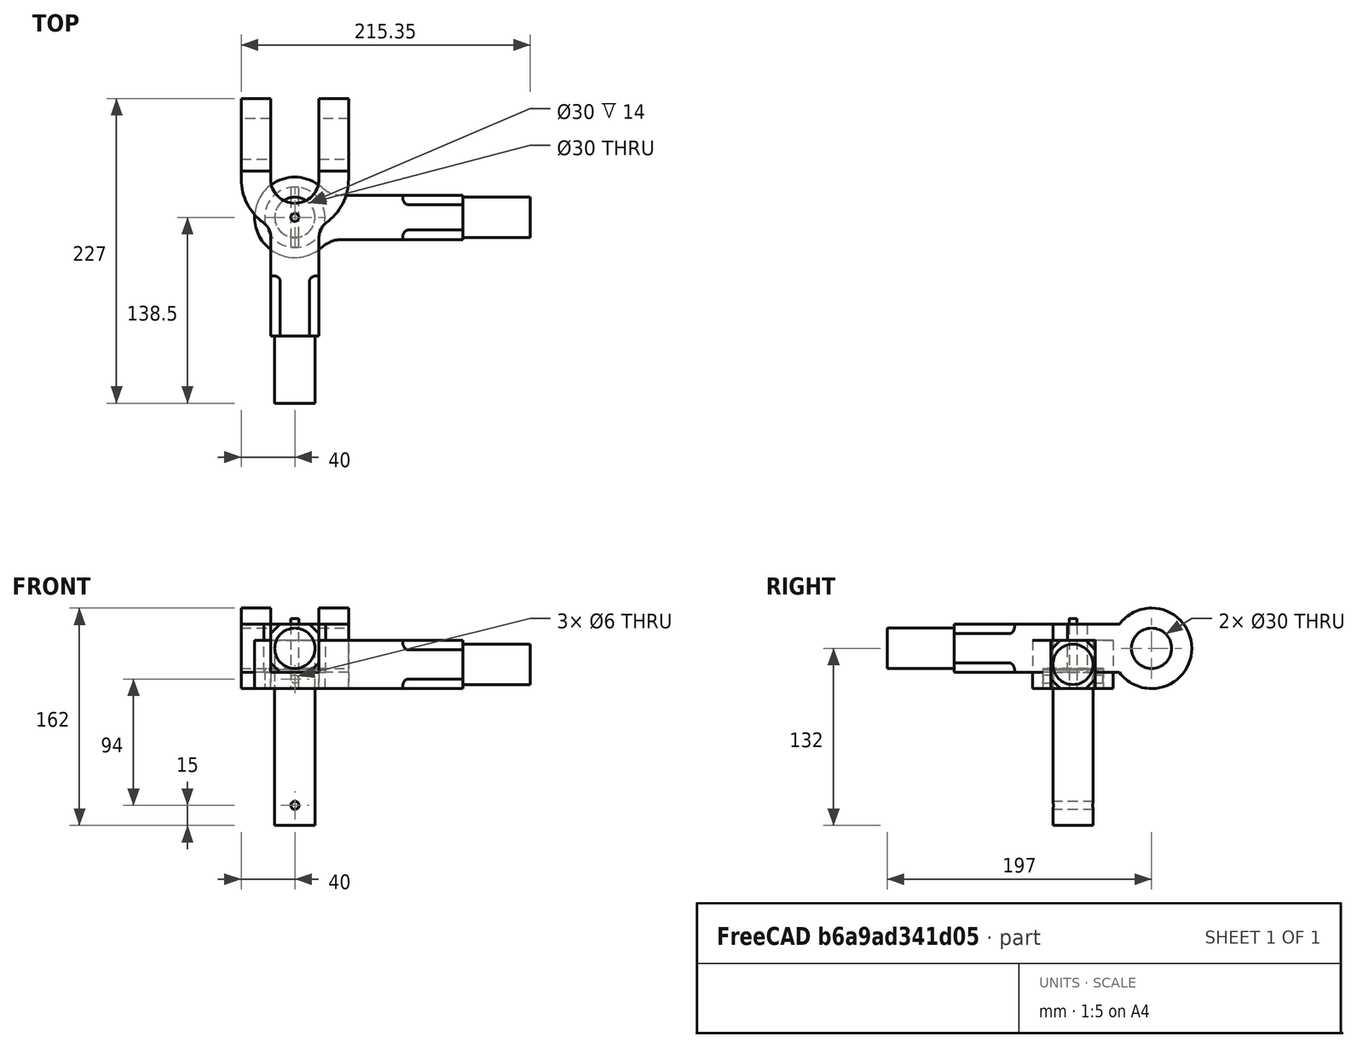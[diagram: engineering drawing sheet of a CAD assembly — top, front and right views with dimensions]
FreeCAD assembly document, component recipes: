
FREECAD ASSEMBLY — COMPONENT RECIPES ("kunckle joint assembly and parts")

This assembly document has 5 components, labeled P0..P4 below (a component is one placed body or linked part). 5 of them carry a construction recipe — the FreeCAD feature program that regenerates the part from scratch, quoted from this document or its linked companion documents; the rest are supplied as boundary geometry only. No exploded tour is included for this assembly.
COMPONENT P0 — recipe-attached ("Collar001", modeled in this document).
Construction recipe (the document's own serialized feature program — sketch geometry with constraints, then the solid features built on it; lengths are millimeters unless a unit is written):

FEATURE [Sketcher::SketchObject] Sketch002
  ArcFitTolerance = 1e-06
  AttachmentSupport = -> [XY_Plane001]
  FullyConstrained = true
  MakeInternals = false
  MapMode = 5
  sketch-geometry (2):
    g0: Circle CenterX=0 CenterY=0 CenterZ=0 NormalX=0 NormalY=0 NormalZ=1 AngleXU=0 Radius=22.5
    g1: Circle CenterX=0 CenterY=0 CenterZ=0 NormalX=0 NormalY=0 NormalZ=1 AngleXU=0 Radius=15
  constraints (4):
    c: Coincident(g0,g-1)
    c: Coincident(g1,g0)
    c: Diameter(g0) = 45
    c: Diameter(g1) = 30
FEATURE [PartDesign::Pad] Pad002
  Direction = (0,0,1)
  Length = 14
  Length2 = 10
  Profile = -> Sketch002
  ReferenceAxis = -> Sketch002 [N_Axis]
  Refine = true
  Suppressed = false
  Type = 0
FEATURE [Sketcher::SketchObject] Sketch003
  ArcFitTolerance = 1e-06
  AttachmentSupport = -> [XZ_Plane001]
  FullyConstrained = true
  MakeInternals = false
  MapMode = 5
  Placement = pos=(0,0,0) rot=(1,0,0;1.5708rad)
  sketch-geometry (1):
    g0: Circle CenterX=0 CenterY=7 CenterZ=0 NormalX=0 NormalY=0 NormalZ=1 AngleXU=0 Radius=3
  constraints (3):
    c: PointOnObject(g0,g-2)
    c: Diameter(g0) = 6
    c: DistanceY(g-1,g0) = 7
FEATURE [PartDesign::Pocket] Pocket
  BaseFeature = -> Pad002
  Direction = (0,1,-2e-16)
  Length = 5
  Length2 = 5
  Midplane = true
  Profile = -> Sketch003
  ReferenceAxis = -> Sketch003 [N_Axis]
  Refine = true
  Suppressed = false
  Type = 1
FEATURE [PartDesign::Body] Body001  label="Collar"
  AllowCompound = false
  Group = -> [Sketch002,Pad002,Sketch003,Pocket]
  Origin = -> Origin001
  Tip = -> Pocket
COMPONENT P1 — recipe-attached ("Single_eye001", modeled in this document).
Construction recipe (the document's own serialized feature program — sketch geometry with constraints, then the solid features built on it; lengths are millimeters unless a unit is written):

FEATURE [Sketcher::SketchObject] Sketch
  ArcFitTolerance = 1e-06
  AttachmentSupport = -> [XY_Plane]
  FullyConstrained = true
  MakeInternals = false
  MapMode = 5
  sketch-geometry (7):
    g0: ArcOfCircle CenterX=0 CenterY=0 CenterZ=0 NormalX=0 NormalY=0 NormalZ=1 AngleXU=0 Radius=30 StartAngle=0.840092 EndAngle=5.44179
    g1: Circle CenterX=0 CenterY=0 CenterZ=0 NormalX=0 NormalY=0 NormalZ=1 AngleXU=0 Radius=15
    g2: LineSegment StartX=35.3005 StartY=-16.5231 StartZ=0 EndX=125.352 EndY=-16.5231 EndZ=0
    g3: LineSegment StartX=125.352 StartY=-16.5231 StartZ=0 EndX=125.352 EndY=16.4769 EndZ=0
    g4: LineSegment StartX=125.352 StartY=16.4769 StartZ=0 EndX=35.3521 EndY=16.4769 EndZ=0
    g5: ArcOfCircle CenterX=35.3521 CenterY=39.4473 CenterZ=0 NormalX=0 NormalY=0 NormalZ=1 AngleXU=0 Radius=22.9703 StartAngle=3.98168 EndAngle=4.71239
    g6: ArcOfCircle CenterX=35.3005 CenterY=-39.4934 CenterZ=0 NormalX=0 NormalY=0 NormalZ=1 AngleXU=0 Radius=22.9703 StartAngle=1.5708 EndAngle=2.30019
  constraints (18):
    c: Coincident(g0,g-1)
    c: Coincident(g1,g0)
    c: Diameter(g1) = 30
    c: Diameter(g0) = 60
    c: Coincident(g2,g3)
    c: Coincident(g3,g4)
    c: Vertical(g3)
    c: Horizontal(g2)
    c: Horizontal(g4)
    c: DistanceY(g3,g3) = 33
    c: Tangent(g0,g5) = 1.5708
    c: Tangent(g4,g5) = 1.5708
    c: Tangent(g0,g6) = 1.5708
    c: Tangent(g2,g6) = 1.5708
    c: Equal(g5,g6)
    c: Block(g5)
    c: Block(g6)
    c: DistanceX(g4,g4) = 90
FEATURE [PartDesign::Pad] Pad
  Direction = (0,0,1)
  Length = 36
  Length2 = 10
  Profile = -> Sketch
  ReferenceAxis = -> Sketch [N_Axis]
  Refine = true
  Suppressed = false
  Type = 0
FEATURE [Sketcher::SketchObject] Sketch001
  ArcFitTolerance = 1e-06
  AttachmentSupport = -> [Pad]
  ExternalGeometry = -> [Pad]
  FullyConstrained = true
  MakeInternals = false
  MapMode = 5
  Placement = pos=(125.352,0,0) rot=(0.57735,0.57735,0.57735;2.0944rad)
  sketch-geometry (1):
    g0: Circle CenterX=-0.0230899 CenterY=18 CenterZ=0 NormalX=0 NormalY=0 NormalZ=1 AngleXU=0 Radius=15
  constraints (2):
    c: Diameter(g0) = 30
    c: Symmetric(g-4,g-3,g0)
FEATURE [PartDesign::Pad] Pad001
  BaseFeature = -> Pad
  Direction = (1,0,0)
  Length = 50
  Length2 = 10
  Profile = -> Sketch001
  ReferenceAxis = -> Sketch001 [N_Axis]
  Refine = true
  Suppressed = false
  Type = 0
FEATURE [Sketcher::SketchObject] Sketch008
  ArcFitTolerance = 1e-06
  AttachmentSupport = -> [Pad001]
  ExternalGeometry = -> [Pad001]
  FullyConstrained = true
  MakeInternals = false
  MapMode = 5
  Placement = pos=(125.352,0,0) rot=(0.57735,0.57735,0.57735;2.0944rad)
  sketch-geometry (12):
    g0: LineSegment StartX=-16.5231 StartY=36 StartZ=0 EndX=-16.5231 EndY=28.9289 EndZ=0
    g1: LineSegment StartX=-16.5231 StartY=28.9289 StartZ=0 EndX=-9.45202 EndY=36 EndZ=0
    g2: LineSegment StartX=-16.5231 StartY=36 StartZ=0 EndX=-9.45202 EndY=36 EndZ=0
    g3: LineSegment StartX=-16.5231 StartY=7.07107 StartZ=0 EndX=-16.5231 EndY=0 EndZ=0
    g4: LineSegment StartX=-16.5231 StartY=0 StartZ=0 EndX=-9.45202 EndY=0 EndZ=0
    g5: LineSegment StartX=-9.45202 StartY=0 StartZ=0 EndX=-16.5231 EndY=7.07107 EndZ=0
    g6: LineSegment StartX=16.5231 StartY=28.9753 StartZ=0 EndX=9.45202 EndY=36 EndZ=0
    g7: LineSegment StartX=16.4769 StartY=36 StartZ=0 EndX=9.45202 EndY=36 EndZ=0
    g8: LineSegment StartX=16.4769 StartY=36 StartZ=0 EndX=16.5231 EndY=28.9753 EndZ=0
    g9: LineSegment StartX=9.40584 StartY=0 StartZ=0 EndX=16.4769 EndY=7.07107 EndZ=0
    g10: LineSegment StartX=16.4769 StartY=7.07107 StartZ=0 EndX=16.4769 EndY=0 EndZ=0
    g11: LineSegment StartX=16.4769 StartY=0 StartZ=0 EndX=9.40584 EndY=0 EndZ=0
  constraints (30):
    c: Coincident(g0,g-5)
    c: PointOnObject(g0,g-5)
    c: Coincident(g1,g0)
    c: Coincident(g2,g0)
    c: Coincident(g2,g1)
    c: PointOnObject(g1,g-3)
    c: PointOnObject(g3,g-5)
    c: Coincident(g3,g-5)
    c: Coincident(g3,g4)
    c: PointOnObject(g4,g-1)
    c: Coincident(g4,g5)
    c: Coincident(g5,g3)
    c: Equal(g2,g0)
    c: Distance(g1,g1) = 10
    c: Distance(g5,g5) = 10
    c: Equal(g3,g4)
    c: Coincident(g6,g8)
    c: Coincident(g7,g8)
    c: Coincident(g7,g6)
    c: Equal(g7,g8)
    c: Coincident(g10,g11)
    c: Coincident(g11,g9)
    c: Coincident(g9,g10)
    c: Equal(g10,g11)
    c: Block(g6)
    c: Coincident(g10,g-4)
    c: PointOnObject(g9,g-1)
    c: Coincident(g7,g-4)
    c: PointOnObject(g9,g-4)
    c: Distance(g9,g9) = 10
FEATURE [PartDesign::Pocket] Pocket002
  BaseFeature = -> Pad001
  Direction = (-1,0,0)
  Length = 45
  Length2 = 5
  Profile = -> Sketch008
  ReferenceAxis = -> Sketch008 [N_Axis]
  Refine = true
  Suppressed = false
  Type = 0
FEATURE [PartDesign::Fillet] Fillet
  Base = -> Pocket002 [Edge46,Edge44]
  BaseFeature = -> Pocket002
  Radius = 4
  Refine = true
  SupportTransform = false
  Suppressed = false
  UseAllEdges = false
FEATURE [PartDesign::Fillet] Fillet001
  Base = -> Fillet [Edge36,Edge52]
  BaseFeature = -> Fillet
  Radius = 4
  Refine = true
  SupportTransform = false
  Suppressed = false
  UseAllEdges = false
FEATURE [PartDesign::Body] Body  label="Single_eye"
  AllowCompound = false
  Group = -> [Sketch,Pad,Sketch001,Pad001,Sketch008,Pocket002,Fillet,Fillet001]
  Origin = -> Origin
  Tip = -> Fillet001
COMPONENT P2 — recipe-attached ("double eye001", modeled in this document).
Construction recipe (the document's own serialized feature program — sketch geometry with constraints, then the solid features built on it; lengths are millimeters unless a unit is written):

FEATURE [Sketcher::SketchObject] Sketch009
  ArcFitTolerance = 1e-06
  AttachmentSupport = -> [XY_Plane004]
  FullyConstrained = true
  MakeInternals = false
  MapMode = 5
  sketch-geometry (5):
    g0: LineSegment StartX=-40 StartY=88.5 StartZ=0 EndX=-40 EndY=-88.5 EndZ=0
    g1: LineSegment StartX=-40 StartY=-88.5 StartZ=0 EndX=40 EndY=-88.5 EndZ=0
    g2: LineSegment StartX=40 StartY=-88.5 StartZ=0 EndX=40 EndY=88.5 EndZ=0
    g3: LineSegment StartX=40 StartY=88.5 StartZ=0 EndX=-40 EndY=88.5 EndZ=0
    g4: GeomPoint [constr] X=0 Y=0 Z=0
  constraints (12):
    c: Coincident(g0,g1)
    c: Coincident(g1,g2)
    c: Coincident(g2,g3)
    c: Coincident(g3,g0)
    c: Vertical(g0)
    c: Vertical(g2)
    c: Horizontal(g1)
    c: Horizontal(g3)
    c: Symmetric(g2,g0,g4)
    c: Coincident(g4,g-1)
    c: DistanceY(g2,g2) = 177
    c: DistanceX(g3,g3) = 80
FEATURE [PartDesign::Pad] Pad006
  Direction = (0,0,1)
  Length = 60
  Length2 = 10
  Profile = -> Sketch009
  ReferenceAxis = -> Sketch009 [N_Axis]
  Refine = true
  Suppressed = false
  Type = 0
FEATURE [PartDesign::Pad] Pad007
  BaseFeature = -> Pad006
  Direction = (0,0,1)
  Length = 5
  Length2 = 10
  Profile = -> Sketch009
  ReferenceAxis = -> Sketch009 [N_Axis]
  Refine = true
  Suppressed = false
  Type = 0
FEATURE [Sketcher::SketchObject] Sketch010
  ArcFitTolerance = 1e-06
  AttachmentSupport = -> [Pad006]
  ExternalGeometry = -> [Pad006]
  FullyConstrained = false
  MakeInternals = false
  MapMode = 5
  Placement = pos=(0,0,0) rot=(1,0,0;3.14159rad)
  sketch-geometry (14):
    g0: ArcOfCircle CenterX=0 CenterY=-28.5 CenterZ=0 NormalX=0 NormalY=0 NormalZ=1 AngleXU=0 Radius=40 StartAngle=-9e-16 EndAngle=0.954279
    g1: ArcOfCircle CenterX=0 CenterY=-28.5 CenterZ=0 NormalX=0 NormalY=0 NormalZ=1 AngleXU=0 Radius=18 StartAngle=2e-16 EndAngle=3.14159
    g2: LineSegment StartX=-18 StartY=88.5 StartZ=0 EndX=-18 EndY=15.1917 EndZ=0
    g3: LineSegment StartX=18 StartY=88.5 StartZ=0 EndX=18 EndY=14.9616 EndZ=0
    g4: LineSegment StartX=-18 StartY=-28.5 StartZ=0 EndX=-18 EndY=-88.5 EndZ=0
    g5: LineSegment StartX=18 StartY=-28.5 StartZ=0 EndX=18 EndY=-88.5 EndZ=0
    g6: LineSegment StartX=-18 StartY=-88.5 StartZ=0 EndX=18 EndY=-88.5 EndZ=0
    g7: LineSegment StartX=-18 StartY=88.5 StartZ=0 EndX=-40 EndY=88.5 EndZ=0
    g8: LineSegment StartX=-40 StartY=88.5 StartZ=0 EndX=-40 EndY=-28.5 EndZ=0
    g9: LineSegment StartX=18 StartY=88.5 StartZ=0 EndX=40 EndY=88.5 EndZ=0
    g10: LineSegment StartX=40 StartY=88.5 StartZ=0 EndX=40 EndY=-28.5 EndZ=0
    g11: ArcOfCircle CenterX=0 CenterY=-28.5 CenterZ=0 NormalX=0 NormalY=0 NormalZ=1 AngleXU=0 Radius=40 StartAngle=2.19011 EndAngle=3.14159
    g12: ArcOfCircle CenterX=31.2806 CenterY=14.625 CenterZ=0 NormalX=0 NormalY=0 NormalZ=1 AngleXU=0 Radius=13.2849 StartAngle=3.11625 EndAngle=4.05167
    g13: ArcOfCircle CenterX=-31.2733 CenterY=14.636 CenterZ=0 NormalX=0 NormalY=0 NormalZ=1 AngleXU=0 Radius=13.2849 StartAngle=5.36376 EndAngle=6.32502
  constraints (33):
    c: Coincident(g1,g0)
    c: Diameter(g1) = 36
    c: PointOnObject(g2,g-5)
    c: Vertical(g2)
    c: PointOnObject(g3,g-5)
    c: Vertical(g3)
    c: PointOnObject(g4,g-6)
    c: Vertical(g4)
    c: PointOnObject(g5,g-6)
    c: Vertical(g5)
    c: Distance(g3,g2) = 36
    c: Distance(g-2,g2) = 18
    c: Tangent(g1,g4) = -1.5708
    c: Tangent(g1,g5) = 1.5708
    c: Coincident(g6,g4)
    c: Coincident(g6,g5)
    c: Coincident(g2,g7)
    c: Coincident(g7,g-5)
    c: Coincident(g7,g8)
    c: Coincident(g3,g9)
    c: Coincident(g9,g-5)
    c: Coincident(g9,g10)
    c: Vertical(g10)
    c: Block(g7)
    c: Block(g8)
    c: Block(g10)
    c: Block(g11)
    c: Block(g0)
    c: Equal(g13,g12)
    c: Coincident(g3,g12)
    c: Coincident(g12,g0)
    c: Coincident(g13,g2)
    c: Coincident(g11,g13)
FEATURE [PartDesign::Pocket] Pocket003
  BaseFeature = -> Pad007
  Direction = (0,0,1)
  Length = 5
  Length2 = 5
  Profile = -> Sketch010
  ReferenceAxis = -> Sketch010 [N_Axis]
  Refine = true
  Suppressed = false
  Type = 1
FEATURE [Sketcher::SketchObject] Sketch011
  ArcFitTolerance = 1e-06
  AttachmentSupport = -> [Pocket003]
  ExternalGeometry = -> [Pocket003]
  FullyConstrained = false
  MakeInternals = false
  MapMode = 5
  Placement = pos=(40,0,0) rot=(0.57735,0.57735,0.57735;2.0944rad)
  sketch-geometry (11):
    g0: ArcOfCircle CenterX=58.5 CenterY=30 CenterZ=0 NormalX=0 NormalY=0 NormalZ=1 AngleXU=0 Radius=30 StartAngle=3.78509 EndAngle=8.78128
    g1: Circle CenterX=58.5 CenterY=30 CenterZ=0 NormalX=0 NormalY=0 NormalZ=1 AngleXU=0 Radius=15
    g2: LineSegment StartX=34.5 StartY=48 StartZ=0 EndX=-88.5 EndY=48 EndZ=0
    g3: LineSegment StartX=-88.5 StartY=12 StartZ=0 EndX=34.5 EndY=12 EndZ=0
    g4: LineSegment StartX=-88.5 StartY=12 StartZ=0 EndX=-88.5 EndY=0 EndZ=0
    g5: LineSegment StartX=-88.5 StartY=0 StartZ=0 EndX=58.5 EndY=0 EndZ=0
    g6: LineSegment StartX=-88.5 StartY=48 StartZ=0 EndX=-88.5 EndY=60 EndZ=0
    g7: LineSegment StartX=-88.5 StartY=60 StartZ=0 EndX=58.5 EndY=60 EndZ=0
    g8: LineSegment StartX=58.5 StartY=60 StartZ=0 EndX=88.5 EndY=60 EndZ=0
    g9: LineSegment StartX=88.5 StartY=60 StartZ=0 EndX=88.5 EndY=0 EndZ=0
    g10: LineSegment StartX=88.5 StartY=0 StartZ=0 EndX=58.5 EndY=0 EndZ=0
  constraints (25):
    c: Coincident(g1,g0)
    c: Diameter(g0) = 60
    c: Diameter(g1) = 30
    c: Tangent(g0,g-4)
    c: Tangent(g-3,g0)
    c: Horizontal(g2)
    c: Horizontal(g3)
    c: Distance(g3,g2) = 36
    c: PointOnObject(g2,g-5)
    c: Coincident(g0,g2)
    c: Coincident(g0,g3)
    c: Coincident(g4,g-5)
    c: Coincident(g4,g5)
    c: PointOnObject(g5,g0)
    c: Horizontal(g5)
    c: Coincident(g6,g2)
    c: Coincident(g6,g-5)
    c: Coincident(g7,g6)
    c: Symmetric(g-3,g-3,g7)
    c: Coincident(g8,g-4)
    c: Horizontal(g8)
    c: Coincident(g8,g9)
    c: Coincident(g9,g-4)
    c: Coincident(g9,g10)
    c: Coincident(g10,g5)
FEATURE [PartDesign::Pocket] Pocket004
  BaseFeature = -> Pocket003
  Direction = (-1,0,0)
  Length = 5
  Length2 = 5
  Profile = -> Sketch011
  ReferenceAxis = -> Sketch011 [N_Axis]
  Refine = true
  Suppressed = false
  Type = 1
FEATURE [Sketcher::SketchObject] Sketch012
  ArcFitTolerance = 1e-06
  AttachmentSupport = -> [Pocket004]
  ExternalGeometry = -> [Pocket004]
  FullyConstrained = true
  MakeInternals = false
  MapMode = 5
  Placement = pos=(0,-88.5,0) rot=(1,0,0;1.5708rad)
  sketch-geometry (1):
    g0: Circle CenterX=2.4e-15 CenterY=30 CenterZ=0 NormalX=0 NormalY=0 NormalZ=1 AngleXU=0 Radius=15
  constraints (2):
    c: Symmetric(g-3,g-4,g0)
    c: Diameter(g0) = 30
FEATURE [PartDesign::Pad] Pad008
  BaseFeature = -> Pocket004
  Direction = (0,-1,2e-16)
  Length = 50
  Length2 = 10
  Profile = -> Sketch012
  ReferenceAxis = -> Sketch012 [N_Axis]
  Refine = true
  Suppressed = false
  Type = 0
FEATURE [Sketcher::SketchObject] Sketch013
  ArcFitTolerance = 1e-06
  AttachmentSupport = -> [Pad008]
  ExternalGeometry = -> [Pad008]
  FullyConstrained = true
  MakeInternals = false
  MapMode = 5
  Placement = pos=(0,-88.5,0) rot=(1,0,0;1.5708rad)
  sketch-geometry (12):
    g0: LineSegment StartX=-18 StartY=48 StartZ=0 EndX=-18 EndY=40.9289 EndZ=0
    g1: LineSegment StartX=-18 StartY=40.9289 StartZ=0 EndX=-10.9289 EndY=48 EndZ=0
    g2: LineSegment StartX=-10.9289 StartY=48 StartZ=0 EndX=-18 EndY=48 EndZ=0
    g3: LineSegment StartX=10.9289 StartY=48 StartZ=0 EndX=18 EndY=40.9289 EndZ=0
    g4: LineSegment StartX=18 StartY=40.9289 StartZ=0 EndX=18 EndY=48 EndZ=0
    g5: LineSegment StartX=18 StartY=48 StartZ=0 EndX=10.9289 EndY=48 EndZ=0
    g6: LineSegment StartX=-18 StartY=19.0711 StartZ=0 EndX=-18 EndY=12 EndZ=0
    g7: LineSegment StartX=-18 StartY=12 StartZ=0 EndX=-10.9289 EndY=12 EndZ=0
    g8: LineSegment StartX=-10.9289 StartY=12 StartZ=0 EndX=-18 EndY=19.0711 EndZ=0
    g9: LineSegment StartX=18 StartY=19.0711 StartZ=0 EndX=18 EndY=12 EndZ=0
    g10: LineSegment StartX=18 StartY=12 StartZ=0 EndX=10.9289 EndY=12 EndZ=0
    g11: LineSegment StartX=10.9289 StartY=12 StartZ=0 EndX=18 EndY=19.0711 EndZ=0
  constraints (32):
    c: Coincident(g-3,g0)
    c: Vertical(g0)
    c: Coincident(g0,g1)
    c: PointOnObject(g1,g-3)
    c: Coincident(g1,g2)
    c: Coincident(g2,g0)
    c: PointOnObject(g3,g-3)
    c: PointOnObject(g3,g-4)
    c: Coincident(g3,g4)
    c: Coincident(g4,g-4)
    c: Coincident(g4,g5)
    c: Coincident(g5,g3)
    c: PointOnObject(g6,g-6)
    c: Coincident(g6,g-6)
    c: Coincident(g6,g7)
    c: PointOnObject(g7,g-5)
    c: Coincident(g7,g8)
    c: Coincident(g8,g6)
    c: PointOnObject(g9,g-4)
    c: Coincident(g9,g-5)
    c: Coincident(g9,g10)
    c: PointOnObject(g10,g-5)
    c: Coincident(g10,g11)
    c: Coincident(g11,g9)
    c: Distance(g1,g1) = 10
    c: Equal(g0,g2)
    c: Equal(g6,g7)
    c: Equal(g10,g9)
    c: Distance(g3,g3) = 10
    c: Distance(g11,g11) = 10
    c: Distance(g8,g8) = 10
    c: Equal(g4,g5)
FEATURE [PartDesign::Pocket] Pocket005
  BaseFeature = -> Pad008
  Direction = (0,1,-2e-16)
  Length = 45
  Length2 = 5
  Profile = -> Sketch013
  ReferenceAxis = -> Sketch013 [N_Axis]
  Refine = true
  Suppressed = false
  Type = 0
FEATURE [PartDesign::Fillet] Fillet002
  Base = -> Pocket005 [Edge83,Edge84,Edge64,Edge72]
  BaseFeature = -> Pocket005
  Radius = 4
  Refine = true
  SupportTransform = false
  Suppressed = false
  UseAllEdges = false
FEATURE [PartDesign::Body] Body004  label="double eye"
  AllowCompound = false
  Group = -> [Sketch009,Pad006,Pad007,Sketch010,Pocket003,Sketch011,Pocket004,Sketch012,Pad008,Sketch013,Pocket005,Fillet002]
  Origin = -> Origin004
  Tip = -> Fillet002
COMPONENT P3 — recipe-attached ("kunckle_pin001", modeled in this document).
Construction recipe (the document's own serialized feature program — sketch geometry with constraints, then the solid features built on it; lengths are millimeters unless a unit is written):

FEATURE [Sketcher::SketchObject] Sketch004
  ArcFitTolerance = 1e-06
  AttachmentSupport = -> [XY_Plane002]
  FullyConstrained = true
  MakeInternals = false
  MapMode = 5
  sketch-geometry (1):
    g0: Circle CenterX=0 CenterY=0 CenterZ=0 NormalX=0 NormalY=0 NormalZ=1 AngleXU=0 Radius=22.5
  constraints (2):
    c: Coincident(g0,g-1)
    c: Diameter(g0) = 45
FEATURE [PartDesign::Pad] Pad003
  Direction = (0,0,1)
  Length = 15
  Length2 = 10
  Profile = -> Sketch004
  ReferenceAxis = -> Sketch004 [N_Axis]
  Refine = true
  Suppressed = false
  Type = 0
FEATURE [Sketcher::SketchObject] Sketch005
  ArcFitTolerance = 1e-06
  AttachmentSupport = -> [Pad003]
  FullyConstrained = true
  MakeInternals = false
  MapMode = 5
  Placement = pos=(0,0,0) rot=(1,0,0;3.14159rad)
  sketch-geometry (1):
    g0: Circle CenterX=0 CenterY=0 CenterZ=0 NormalX=0 NormalY=0 NormalZ=1 AngleXU=0 Radius=15
  constraints (2):
    c: Coincident(g0,g-1)
    c: Diameter(g0) = 30
FEATURE [PartDesign::Pad] Pad004
  BaseFeature = -> Pad003
  Direction = (0,0,-1)
  Length = 102
  Length2 = 10
  Profile = -> Sketch005
  ReferenceAxis = -> Sketch005 [N_Axis]
  Refine = true
  Suppressed = false
  Type = 0
FEATURE [Sketcher::SketchObject] Sketch006
  ArcFitTolerance = 1e-06
  AttachmentSupport = -> [XZ_Plane002]
  ExternalGeometry = -> [Pad004]
  FullyConstrained = true
  MakeInternals = false
  MapMode = 5
  Placement = pos=(0,0,0) rot=(1,0,0;1.5708rad)
  sketch-geometry (1):
    g0: Circle CenterX=0 CenterY=-87 CenterZ=0 NormalX=0 NormalY=0 NormalZ=1 AngleXU=0 Radius=3
  constraints (3):
    c: PointOnObject(g0,g-2)
    c: Diameter(g0) = 6
    c: Distance(g0,g-3) = 15
FEATURE [PartDesign::Pocket] Pocket001
  BaseFeature = -> Pad004
  Direction = (0,1,-2e-16)
  Length = 5
  Length2 = 5
  Midplane = true
  Profile = -> Sketch006
  ReferenceAxis = -> Sketch006 [N_Axis]
  Refine = true
  Suppressed = false
  Type = 1
FEATURE [PartDesign::Body] Body002  label="kunckle_pin"
  AllowCompound = false
  Group = -> [Sketch004,Pad003,Sketch005,Pad004,Sketch006,Pocket001]
  Origin = -> Origin002
  Tip = -> Pocket001
COMPONENT P4 — recipe-attached ("taper_pin001", modeled in this document).
Construction recipe (the document's own serialized feature program — sketch geometry with constraints, then the solid features built on it; lengths are millimeters unless a unit is written):

FEATURE [Sketcher::SketchObject] Sketch007
  ArcFitTolerance = 1e-06
  AttachmentSupport = -> [XY_Plane003]
  FullyConstrained = true
  MakeInternals = false
  MapMode = 5
  sketch-geometry (1):
    g0: Circle CenterX=0 CenterY=0 CenterZ=0 NormalX=0 NormalY=0 NormalZ=1 AngleXU=0 Radius=3
  constraints (2):
    c: Coincident(g0,g-1)
    c: Diameter(g0) = 6
FEATURE [PartDesign::Pad] Pad005
  Direction = (0,0,1)
  Length = 52
  Length2 = 10
  Profile = -> Sketch007
  ReferenceAxis = -> Sketch007 [N_Axis]
  Refine = true
  Suppressed = false
  Type = 0
FEATURE [PartDesign::Body] Body003  label="taper_pin"
  AllowCompound = false
  Group = -> [Sketch007,Pad005]
  Origin = -> Origin003
  Tip = -> Pad005
PROVENANCE & LICENSES
A FreeCAD (.FCStd) document from a public repository crawl; recipes are the document's own serialized feature recipes (and, for linked parts, companion documents' recipes).
License: as declared in the source repository (recorded in the dataset sidecar).
